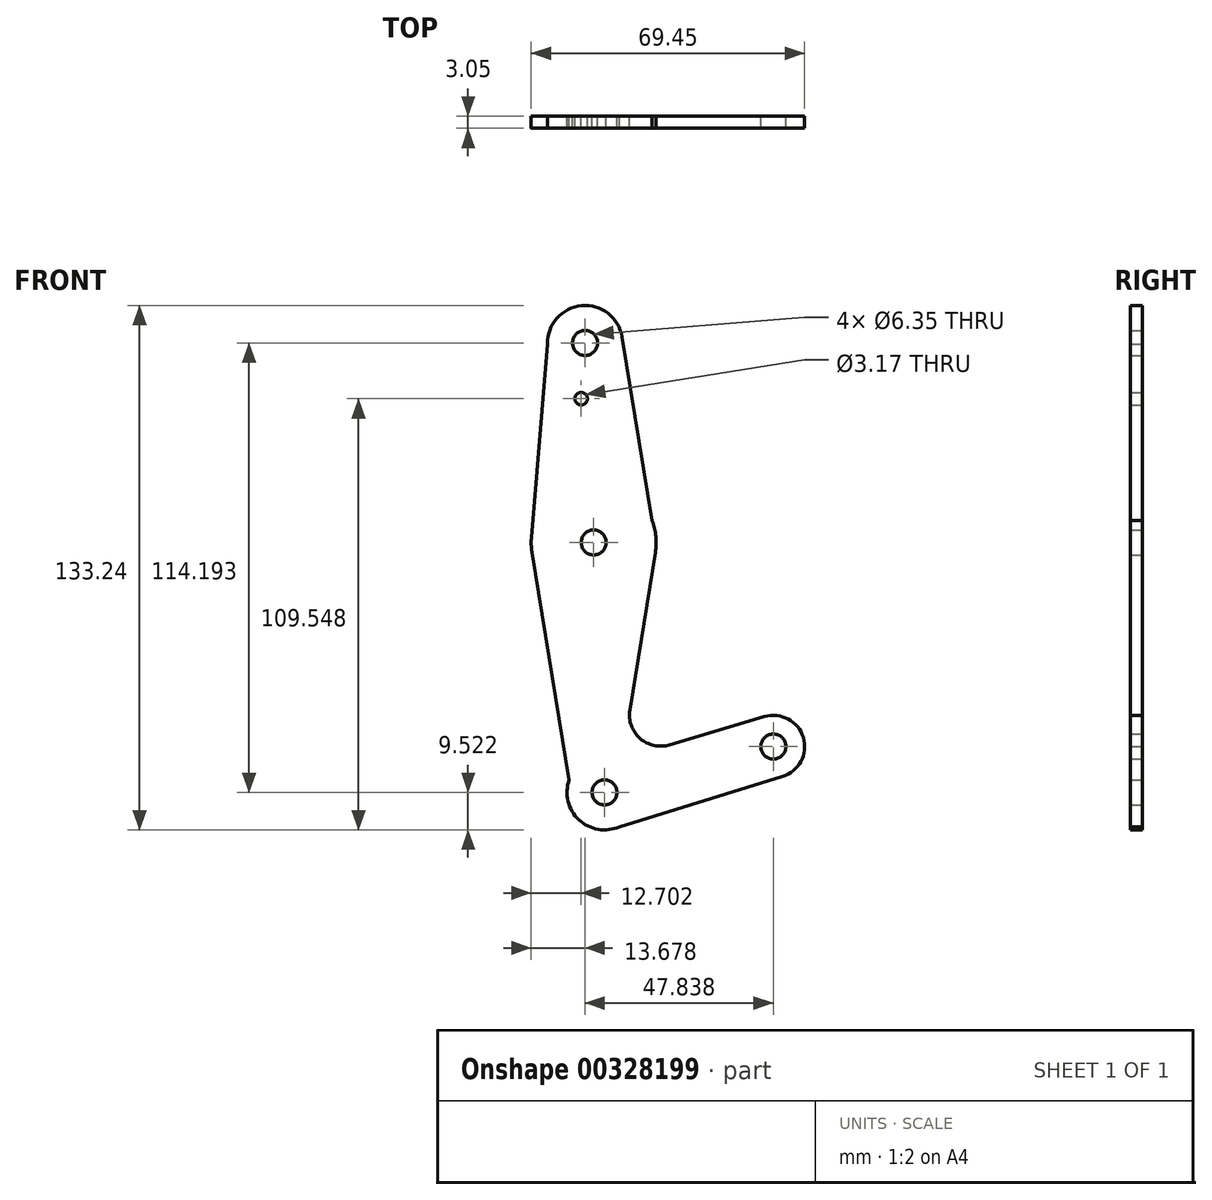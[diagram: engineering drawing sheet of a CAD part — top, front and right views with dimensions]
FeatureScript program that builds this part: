
annotation { "Feature Type Name" : "Feature", "Feature Type Description" : "" }
export const myFeature = defineFeature(function(context is Context, id is Id, definition is map)
    precondition{}
    {
        {
            var Q0;
            Q0=qCreatedBy(makeId("Front.planeOp"),FACE);
            var sketch = newSketch(context, id + "F0", { "sketchPlane" : qUnion([Q0])});
            skLineSegment(sketch, "E0", {"start": v(-1.46, 337.79) * mm, "end": v(3.48, 223.6) * mm, "construction": true});
            skLineSegment(sketch, "E1", {"start": v(3.48, 223.6) * mm, "end": v(46.38, 235.23) * mm, "construction": true});
            skCircle(sketch, "E2", {"center": v(-1.46, 337.79) * mm, "radius": 9.53 * mm});
            skCircle(sketch, "E3", {"center": v(46.38, 235.23) * mm, "radius": 7.94 * mm});
            skCircle(sketch, "E4", {"center": v(3.48, 223.6) * mm, "radius": 9.53 * mm});
            skCircle(sketch, "E5", {"center": v(0.73, 287.1) * mm, "radius": 15.88 * mm});
            skLineSegment(sketch, "E6", {"start": v(-10.98, 337.53) * mm, "end": v(-15.09, 288.41) * mm});
            skLineSegment(sketch, "E7", {"start": v(5.2, 214.22) * mm, "end": v(48.72, 227.65) * mm});
            skLineSegment(sketch, "E8", {"start": v(7.94, 339.33) * mm, "end": v(16.6, 286.57) * mm});
            skCircle(sketch, "E9", {"center": v(-1.46, 337.79) * mm, "radius": 3.18 * mm});
            skCircle(sketch, "E10", {"center": v(0.73, 287.1) * mm, "radius": 3.18 * mm});
            skCircle(sketch, "E11", {"center": v(3.48, 223.6) * mm, "radius": 3.18 * mm});
            skCircle(sketch, "E12", {"center": v(46.38, 235.23) * mm, "radius": 3.18 * mm});
            skCircle(sketch, "E13", {"center": v(-2.44, 323.62) * mm, "radius": 1.59 * mm});
            skLineSegment(sketch, "E14", {"start": v(16.4, 284.55) * mm, "end": v(9.92, 244.55) * mm});
            skLineSegment(sketch, "E15", {"start": v(20.04, 235.66) * mm, "end": v(44.1, 242.84) * mm});
            skLineSegment(sketch, "E16", {"start": v(-14.94, 284.53) * mm, "end": v(-5.49, 226.81) * mm});
            skPoint(sketch, "E17.visualSharp", {"position": v(7.89, 232.04) * mm});
            skArc(sketch, "E17.filletArc", {"start": v(9.92, 244.55) * mm, "mid": v(12.52, 237.3) * mm, "end": v(20.04, 235.66) * mm});
            skSolve(sketch);
        }
        {
            var Q0;
            Q0 = qSketchRegion(id + "F0", true);
            extrude(context, id + "F1", {"entities" : qUnion([Q0]), "depth" : 3.05 * mm});
        }
    });
